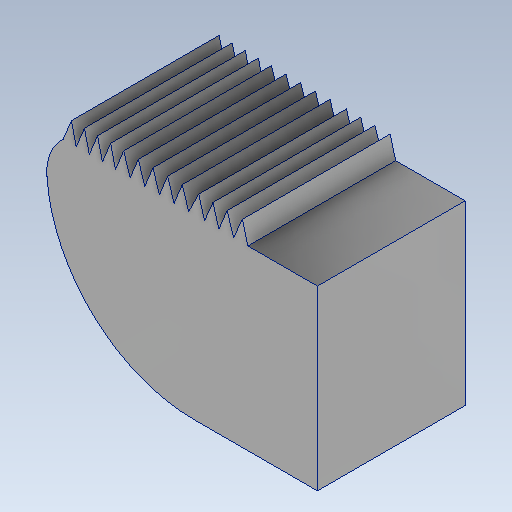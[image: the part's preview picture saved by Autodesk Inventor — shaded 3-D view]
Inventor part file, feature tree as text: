
AUTODESK INVENTOR PART (.ipt)
format: ipt  version: 2025.2 (Build 292293000, 293)  size: 388,608 bytes
history: native  units: mm
features: fillet x2, extrude x1, sketch x1
ambient origin geometry x8: Origin, YZ Plane, XZ Plane, XY Plane, X Axis, Y Axis, Z Axis, Center Point
bodies: Solid2 (feature_tree)
feature tree (4):
  extrude  "Extrusion2"  Depth=27.5mm
  fillet  "Fillet2"  Radius=18.0mm
  fillet  "Rundung3"  Radius=15.0mm
  sketch  "Sketch5"  dims[d56=15.0mm d57=0.0mm d67=15.6mm d97=18.0mm d98=15.0mm d105=5.0mm d106=27.5mm d139=2.055345mm]
